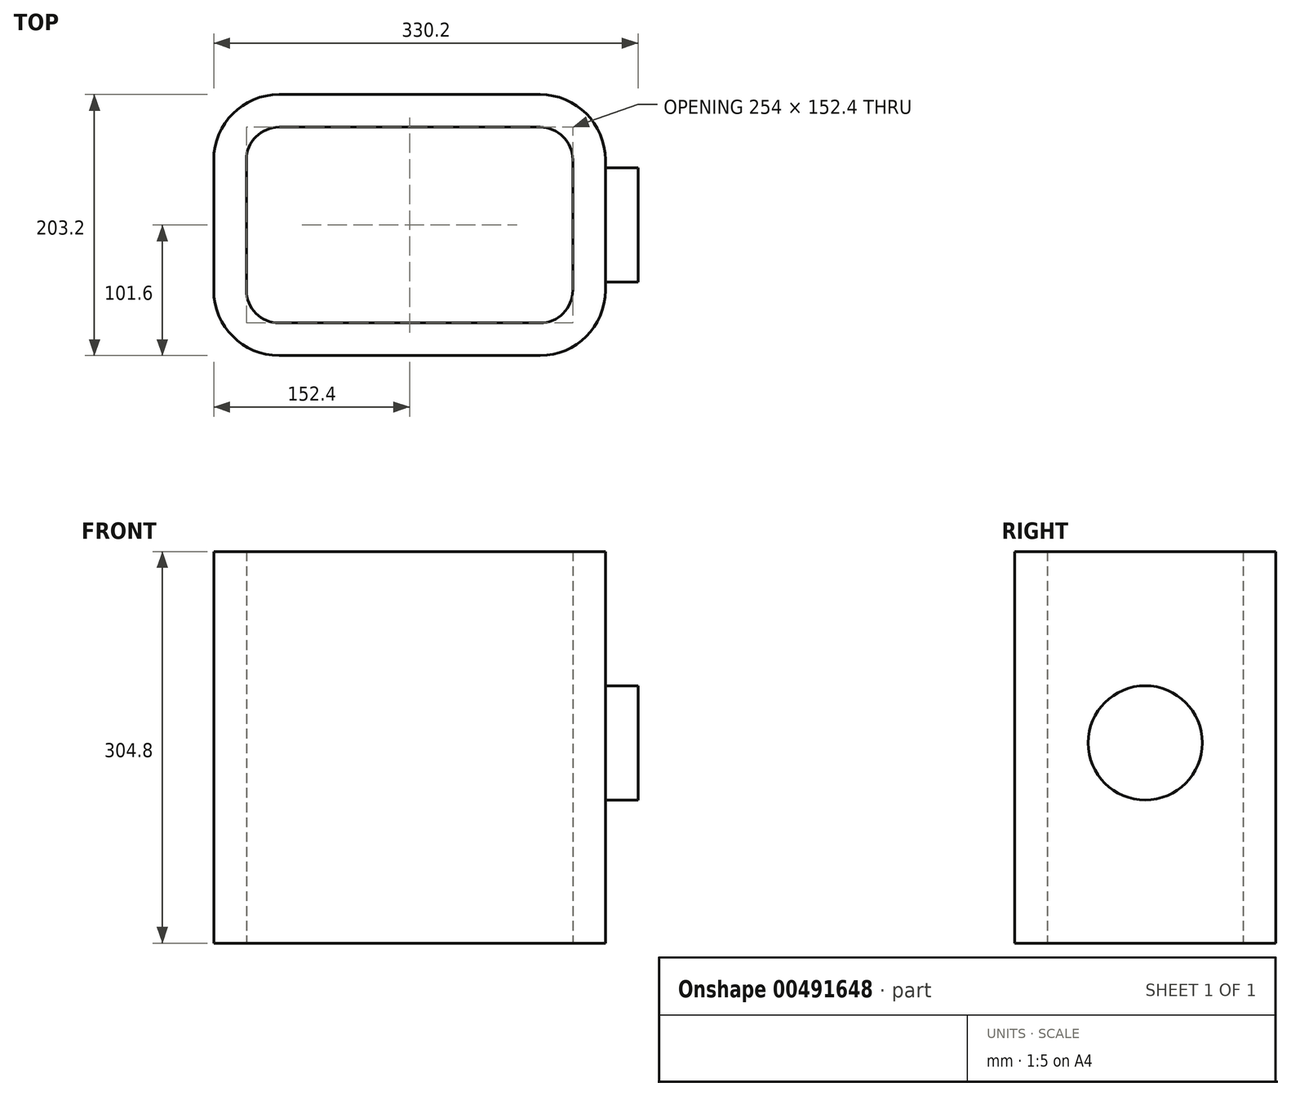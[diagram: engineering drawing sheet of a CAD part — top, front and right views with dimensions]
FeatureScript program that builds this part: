
annotation { "Feature Type Name" : "Feature", "Feature Type Description" : "" }
export const myFeature = defineFeature(function(context is Context, id is Id, definition is map)
    precondition{}
    {
        {
            var Q0;
            Q0=qCreatedBy(makeId("Top.planeOp"),FACE);
            var sketch = newSketch(context, id + "F0", { "sketchPlane" : qUnion([Q0])});
            skLineSegment(sketch, "E0.bottom", {"start": v(101.6, 76.2) * mm, "end": v(-101.6, 76.2) * mm});
            skLineSegment(sketch, "E0.top", {"start": v(101.6, -76.2) * mm, "end": v(-101.6, -76.2) * mm});
            skLineSegment(sketch, "E0.left", {"start": v(127, 50.8) * mm, "end": v(127, -50.8) * mm});
            skLineSegment(sketch, "E0.right", {"start": v(-127, 50.8) * mm, "end": v(-127, -50.8) * mm});
            skPoint(sketch, "E0.middle", {"position": v(0, 0) * mm});
            skPoint(sketch, "E1.visualSharp", {"position": v(-127, -76.2) * mm});
            skArc(sketch, "E1.filletArc", {"start": v(-127, -50.8) * mm, "mid": v(-119.56, -68.76) * mm, "end": v(-101.6, -76.2) * mm});
            skPoint(sketch, "E2.visualSharp", {"position": v(127, 76.2) * mm});
            skArc(sketch, "E2.filletArc", {"start": v(127, 50.8) * mm, "mid": v(119.56, 68.76) * mm, "end": v(101.6, 76.2) * mm});
            skPoint(sketch, "E3.visualSharp", {"position": v(127, -76.2) * mm});
            skArc(sketch, "E3.filletArc", {"start": v(101.6, -76.2) * mm, "mid": v(119.56, -68.76) * mm, "end": v(127, -50.8) * mm});
            skPoint(sketch, "E4.visualSharp", {"position": v(-127, 76.2) * mm});
            skArc(sketch, "E4.filletArc", {"start": v(-101.6, 76.2) * mm, "mid": v(-119.56, 68.76) * mm, "end": v(-127, 50.8) * mm});
            skArc(sketch, "E5.0", {"start": v(152.4, 50.8) * mm, "mid": v(137.52, 86.72) * mm, "end": v(101.6, 101.6) * mm});
            skLineSegment(sketch, "E5.1", {"start": v(152.4, 50.8) * mm, "end": v(152.4, -50.8) * mm});
            skLineSegment(sketch, "E5.2", {"start": v(101.6, 101.6) * mm, "end": v(-101.6, 101.6) * mm});
            skArc(sketch, "E5.3", {"start": v(101.6, -101.6) * mm, "mid": v(137.52, -86.72) * mm, "end": v(152.4, -50.8) * mm});
            skArc(sketch, "E5.4", {"start": v(-101.6, 101.6) * mm, "mid": v(-137.52, 86.72) * mm, "end": v(-152.4, 50.8) * mm});
            skLineSegment(sketch, "E5.5", {"start": v(-152.4, 50.8) * mm, "end": v(-152.4, -50.8) * mm});
            skArc(sketch, "E5.6", {"start": v(-152.4, -50.8) * mm, "mid": v(-137.52, -86.72) * mm, "end": v(-101.6, -101.6) * mm});
            skLineSegment(sketch, "E5.7", {"start": v(101.6, -101.6) * mm, "end": v(-101.6, -101.6) * mm});
            skSolve(sketch);
        }
        {
            var Q0;
            Q0=makeQuery(id+"F0.imprint","IMPRINT",FACE,{"disambiguationData":[TD([[makeQuery(id+"F0.imprint","IMPRINT",EDGE,{"derivedFrom":sQuery(id+"F0.wireOp",EDGE,"E0.bottom")}),-1.0]])]});
            extrude(context, id + "F1", {"entities" : qUnion([Q0]), "depth" : 304.8 * mm});
        }
        {
            var Q0;
            Q0=makeQuery(id+"F1.opExtrude","SWEPT_FACE",FACE,{"disambiguationData":[OSD([sQuery(id+"F0.wireOp",EDGE,"E5.1")])]});
            var sketch = newSketch(context, id + "F2", { "sketchPlane" : qUnion([Q0])});
            skCircle(sketch, "E6", {"center": v(0, 155.89) * mm, "radius": 44.45 * mm});
            skSolve(sketch);
        }
        {
            var Q0;
            Q0 = qSketchRegion(id + "F2", true);
            extrude(context, id + "F3", {"entities" : qUnion([Q0]), "depth" : 25.4 * mm, "offsetDistance" : 25.4 * mm});
        }
    });
